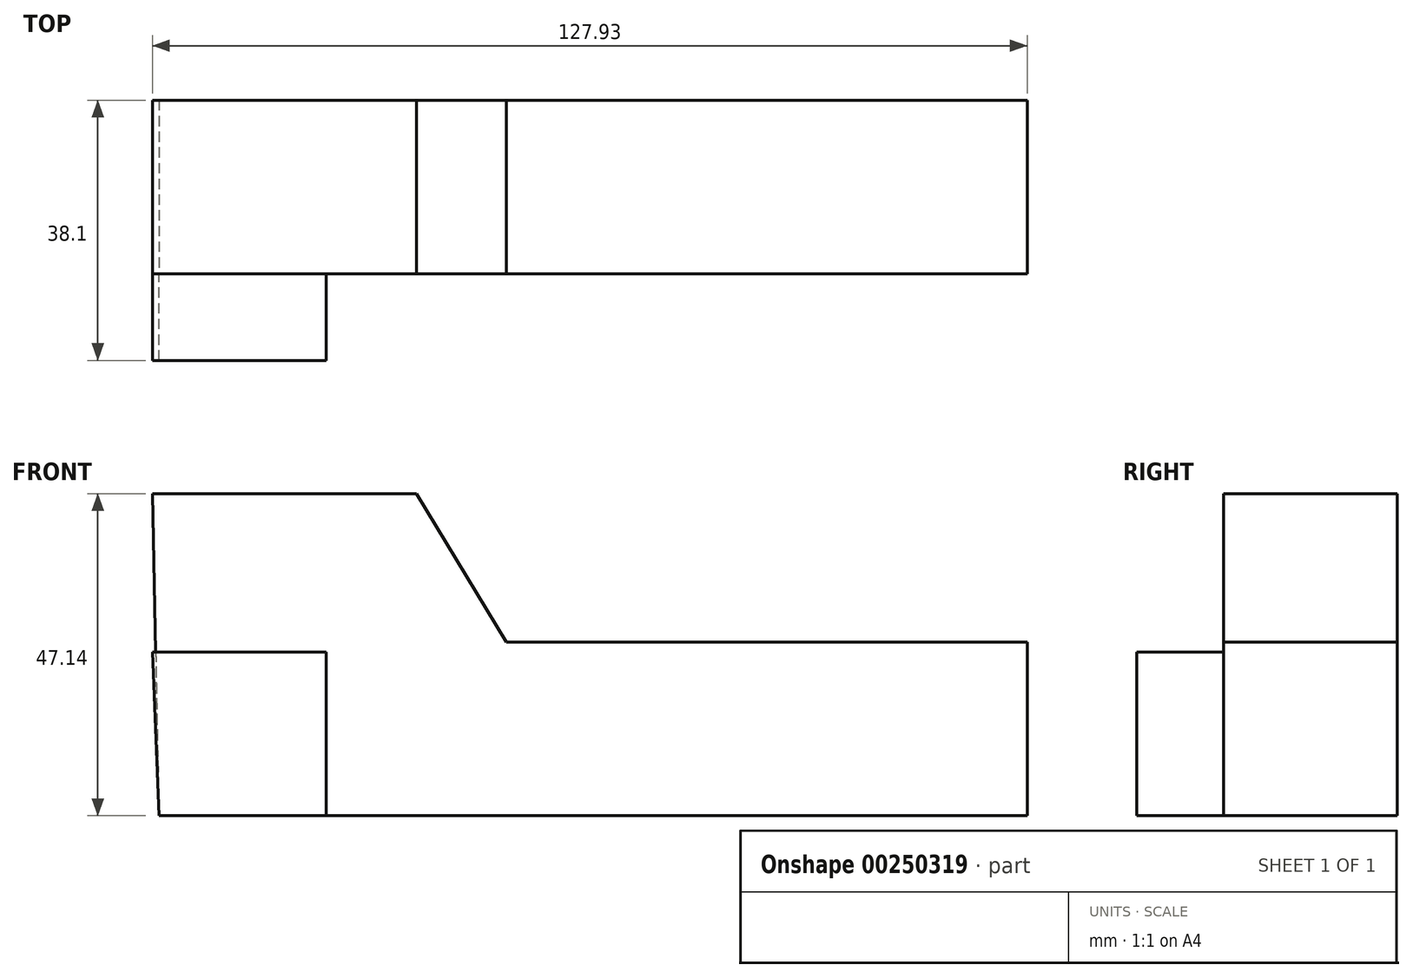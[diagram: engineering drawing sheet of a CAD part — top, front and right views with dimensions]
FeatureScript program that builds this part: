
annotation { "Feature Type Name" : "Feature", "Feature Type Description" : "" }
export const myFeature = defineFeature(function(context is Context, id is Id, definition is map)
    precondition{}
    {
        {
            var Q0;
            Q0=qCreatedBy(makeId("Front.planeOp"),FACE);
            var sketch = newSketch(context, id + "F0", { "sketchPlane" : qUnion([Q0])});
            skLineSegment(sketch, "E0", {"start": v(-70.88, 0) * mm, "end": v(56.12, 0) * mm});
            skLineSegment(sketch, "E1", {"start": v(56.12, 0) * mm, "end": v(56.12, 25.4) * mm});
            skLineSegment(sketch, "E2", {"start": v(56.12, 25.4) * mm, "end": v(-20.08, 25.4) * mm});
            skLineSegment(sketch, "E3", {"start": v(-20.08, 25.4) * mm, "end": v(-33.2, 47.14) * mm});
            skLineSegment(sketch, "E4", {"start": v(-33.2, 47.14) * mm, "end": v(-71.8, 47.14) * mm});
            skLineSegment(sketch, "E5", {"start": v(-71.8, 47.14) * mm, "end": v(-70.88, 0) * mm});
            skSolve(sketch);
        }
        {
            var Q0;
            Q0=makeQuery(id+"F0.imprint","IMPRINT",FACE,{"disambiguationData":[TD([[makeQuery(id+"F0.imprint","IMPRINT",EDGE,{"derivedFrom":sQuery(id+"F0.wireOp",EDGE,"E0")}),1.0]])]});
            extrude(context, id + "F1", {"entities" : qUnion([Q0]), "oppositeDirection" : true, "depth" : 25.4 * mm});
        }
        {
            var Q0;
            Q0=qCreatedBy(makeId("Front.planeOp"),FACE);
            var sketch = newSketch(context, id + "F2", { "sketchPlane" : qUnion([Q0])});
            skLineSegment(sketch, "E6", {"start": v(-71.8, 23.99) * mm, "end": v(-46.4, 23.99) * mm});
            skLineSegment(sketch, "E7", {"start": v(-46.4, 23.99) * mm, "end": v(-46.4, 0) * mm});
            skLineSegment(sketch, "E8", {"start": v(-46.4, 0) * mm, "end": v(-70.88, 0) * mm});
            skLineSegment(sketch, "E9", {"start": v(-70.88, 0) * mm, "end": v(-71.8, 23.99) * mm});
            skSolve(sketch);
        }
        {
            var Q0;
            Q0=makeQuery(id+"F2.imprint","IMPRINT",FACE,{"disambiguationData":[TD([[makeQuery(id+"F2.imprint","IMPRINT",EDGE,{"derivedFrom":sQuery(id+"F2.wireOp",EDGE,"E6")}),-1.0]])]});
            extrude(context, id + "F3", {"entities" : qUnion([Q0]), "operationType" : NewBodyOperationType.ADD, "depth" : 12.7 * mm});
        }
    });
